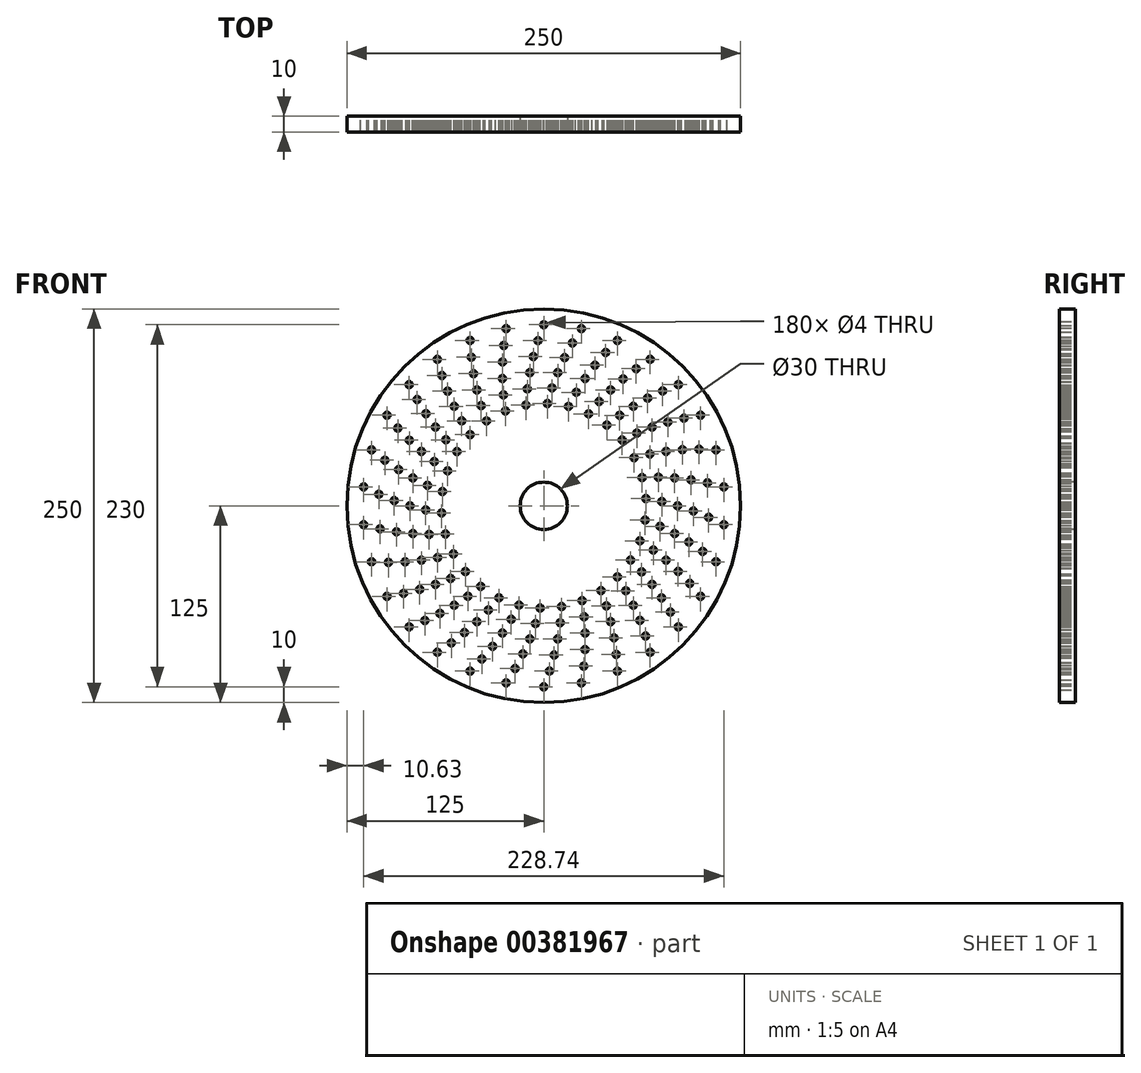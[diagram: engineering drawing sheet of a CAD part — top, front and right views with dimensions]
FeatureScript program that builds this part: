
annotation { "Feature Type Name" : "Feature", "Feature Type Description" : "" }
export const myFeature = defineFeature(function(context is Context, id is Id, definition is map)
    precondition{}
    {
        {
            var Q0;
            Q0=qCreatedBy(makeId("Front.planeOp"),FACE);
            var sketch = newSketch(context, id + "F0", { "sketchPlane" : qUnion([Q0])});
            skCircle(sketch, "E0", {"center": v(0, 0) * mm, "radius": 125 * mm});
            skCircle(sketch, "E1", {"center": v(0, 0) * mm, "radius": 115 * mm, "construction": true});
            skLineSegment(sketch, "E2", {"start": v(0, 125) * mm, "end": v(0, -125) * mm, "construction": true});
            skCircle(sketch, "E3", {"center": v(0, 115) * mm, "radius": 2 * mm});
            skCircle(sketch, "E4", {"center": v(0, 0) * mm, "radius": 105 * mm, "construction": true});
            skCircle(sketch, "E5", {"center": v(0, 0) * mm, "radius": 95 * mm, "construction": true});
            skCircle(sketch, "E6", {"center": v(0, 0) * mm, "radius": 85 * mm, "construction": true});
            skCircle(sketch, "E7", {"center": v(0, 0) * mm, "radius": 75 * mm, "construction": true});
            skCircle(sketch, "E8", {"center": v(0, 0) * mm, "radius": 65 * mm, "construction": true});
            skLineSegment(sketch, "E9", {"start": v(0, 0) * mm, "end": v(-3.66, 104.94) * mm, "construction": true});
            skLineSegment(sketch, "E10", {"start": v(0, 0) * mm, "end": v(-6.63, 94.77) * mm, "construction": true});
            skLineSegment(sketch, "E11", {"start": v(0, 0) * mm, "end": v(-8.88, 84.53) * mm, "construction": true});
            skLineSegment(sketch, "E12", {"start": v(0, 0) * mm, "end": v(-10.44, 74.27) * mm, "construction": true});
            skLineSegment(sketch, "E13", {"start": v(0, 0) * mm, "end": v(-11.29, 64.01) * mm, "construction": true});
            skCircle(sketch, "E14", {"center": v(-3.66, 104.94) * mm, "radius": 2 * mm});
            skCircle(sketch, "E15", {"center": v(-6.63, 94.77) * mm, "radius": 2 * mm});
            skCircle(sketch, "E16", {"center": v(-8.88, 84.53) * mm, "radius": 2 * mm});
            skCircle(sketch, "E17", {"center": v(-10.44, 74.27) * mm, "radius": 2 * mm});
            skCircle(sketch, "E18", {"center": v(-11.29, 64.01) * mm, "radius": 2 * mm});
            skCircle(sketch, "E19.1.0", {"center": v(-23.9, 112.49) * mm, "radius": 2 * mm});
            skCircle(sketch, "E19.1.1", {"center": v(-25.4, 101.88) * mm, "radius": 2 * mm});
            skCircle(sketch, "E19.1.2", {"center": v(-26.19, 91.32) * mm, "radius": 2 * mm});
            skCircle(sketch, "E19.1.3", {"center": v(-26.27, 80.84) * mm, "radius": 2 * mm});
            skCircle(sketch, "E19.1.4", {"center": v(-25.65, 70.48) * mm, "radius": 2 * mm});
            skCircle(sketch, "E19.1.5", {"center": v(-24.35, 60.27) * mm, "radius": 2 * mm});
            skCircle(sketch, "E19.2.0", {"center": v(-46.77, 105.06) * mm, "radius": 2 * mm});
            skCircle(sketch, "E19.2.1", {"center": v(-46.03, 94.37) * mm, "radius": 2 * mm});
            skCircle(sketch, "E19.2.2", {"center": v(-44.6, 83.88) * mm, "radius": 2 * mm});
            skCircle(sketch, "E19.2.3", {"center": v(-42.5, 73.61) * mm, "radius": 2 * mm});
            skCircle(sketch, "E19.2.4", {"center": v(-39.74, 63.6) * mm, "radius": 2 * mm});
            skCircle(sketch, "E19.2.5", {"center": v(-36.35, 53.89) * mm, "radius": 2 * mm});
            skCircle(sketch, "E19.3.0", {"center": v(-67.6, 93.04) * mm, "radius": 2 * mm});
            skCircle(sketch, "E19.3.1", {"center": v(-64.64, 82.74) * mm, "radius": 2 * mm});
            skCircle(sketch, "E19.3.2", {"center": v(-61.06, 72.77) * mm, "radius": 2 * mm});
            skCircle(sketch, "E19.3.3", {"center": v(-56.88, 63.17) * mm, "radius": 2 * mm});
            skCircle(sketch, "E19.3.4", {"center": v(-52.1, 53.95) * mm, "radius": 2 * mm});
            skCircle(sketch, "E19.3.5", {"center": v(-46.76, 45.15) * mm, "radius": 2 * mm});
            skCircle(sketch, "E19.4.0", {"center": v(-85.46, 76.95) * mm, "radius": 2 * mm});
            skCircle(sketch, "E19.4.1", {"center": v(-80.43, 67.5) * mm, "radius": 2 * mm});
            skCircle(sketch, "E19.4.2", {"center": v(-74.86, 58.49) * mm, "radius": 2 * mm});
            skCircle(sketch, "E19.4.3", {"center": v(-68.77, 49.96) * mm, "radius": 2 * mm});
            skCircle(sketch, "E19.4.4", {"center": v(-62.18, 41.94) * mm, "radius": 2 * mm});
            skCircle(sketch, "E19.4.5", {"center": v(-55.12, 34.44) * mm, "radius": 2 * mm});
            skCircle(sketch, "E19.5.0", {"center": v(-99.6, 57.5) * mm, "radius": 2 * mm});
            skCircle(sketch, "E19.5.1", {"center": v(-92.7, 49.3) * mm, "radius": 2 * mm});
            skCircle(sketch, "E19.5.2", {"center": v(-85.39, 41.65) * mm, "radius": 2 * mm});
            skCircle(sketch, "E19.5.3", {"center": v(-77.65, 34.57) * mm, "radius": 2 * mm});
            skCircle(sketch, "E19.5.4", {"center": v(-69.54, 28.1) * mm, "radius": 2 * mm});
            skCircle(sketch, "E19.5.5", {"center": v(-61.08, 22.23) * mm, "radius": 2 * mm});
            skCircle(sketch, "E19.6.0", {"center": v(-109.37, 35.54) * mm, "radius": 2 * mm});
            skCircle(sketch, "E19.6.1", {"center": v(-100.93, 28.94) * mm, "radius": 2 * mm});
            skCircle(sketch, "E19.6.2", {"center": v(-92.18, 22.98) * mm, "radius": 2 * mm});
            skCircle(sketch, "E19.6.3", {"center": v(-83.14, 17.67) * mm, "radius": 2 * mm});
            skCircle(sketch, "E19.6.4", {"center": v(-73.86, 13.02) * mm, "radius": 2 * mm});
            skCircle(sketch, "E19.6.5", {"center": v(-64.37, 9.05) * mm, "radius": 2 * mm});
            skCircle(sketch, "E19.7.0", {"center": v(-114.37, 12.02) * mm, "radius": 2 * mm});
            skCircle(sketch, "E19.7.1", {"center": v(-104.74, 7.32) * mm, "radius": 2 * mm});
            skCircle(sketch, "E19.7.2", {"center": v(-94.94, 3.32) * mm, "radius": 2 * mm});
            skCircle(sketch, "E19.7.3", {"center": v(-85, 0) * mm, "radius": 2 * mm});
            skCircle(sketch, "E19.7.4", {"center": v(-74.95, -2.62) * mm, "radius": 2 * mm});
            skCircle(sketch, "E19.7.5", {"center": v(-64.84, -4.53) * mm, "radius": 2 * mm});
            skCircle(sketch, "E19.8.0", {"center": v(-114.37, -12.02) * mm, "radius": 2 * mm});
            skCircle(sketch, "E19.8.1", {"center": v(-103.98, -14.61) * mm, "radius": 2 * mm});
            skCircle(sketch, "E19.8.2", {"center": v(-93.56, -16.5) * mm, "radius": 2 * mm});
            skCircle(sketch, "E19.8.3", {"center": v(-83.14, -17.67) * mm, "radius": 2 * mm});
            skCircle(sketch, "E19.8.4", {"center": v(-72.77, -18.14) * mm, "radius": 2 * mm});
            skCircle(sketch, "E19.8.5", {"center": v(-62.48, -17.92) * mm, "radius": 2 * mm});
            skCircle(sketch, "E19.9.0", {"center": v(-109.37, -35.54) * mm, "radius": 2 * mm});
            skCircle(sketch, "E19.9.1", {"center": v(-98.67, -35.91) * mm, "radius": 2 * mm});
            skCircle(sketch, "E19.9.2", {"center": v(-88.08, -35.59) * mm, "radius": 2 * mm});
            skCircle(sketch, "E19.9.3", {"center": v(-77.65, -34.57) * mm, "radius": 2 * mm});
            skCircle(sketch, "E19.9.4", {"center": v(-67.4, -32.88) * mm, "radius": 2 * mm});
            skCircle(sketch, "E19.9.5", {"center": v(-57.4, -30.52) * mm, "radius": 2 * mm});
            skCircle(sketch, "E19.10.0", {"center": v(-99.6, -57.5) * mm, "radius": 2 * mm});
            skCircle(sketch, "E19.10.1", {"center": v(-89.05, -55.64) * mm, "radius": 2 * mm});
            skCircle(sketch, "E19.10.2", {"center": v(-78.76, -53.12) * mm, "radius": 2 * mm});
            skCircle(sketch, "E19.10.3", {"center": v(-68.77, -49.96) * mm, "radius": 2 * mm});
            skCircle(sketch, "E19.10.4", {"center": v(-59.1, -46.17) * mm, "radius": 2 * mm});
            skCircle(sketch, "E19.10.5", {"center": v(-49.8, -41.78) * mm, "radius": 2 * mm});
            skCircle(sketch, "E19.11.0", {"center": v(-85.46, -76.95) * mm, "radius": 2 * mm});
            skCircle(sketch, "E19.11.1", {"center": v(-75.53, -72.94) * mm, "radius": 2 * mm});
            skCircle(sketch, "E19.11.2", {"center": v(-66, -68.34) * mm, "radius": 2 * mm});
            skCircle(sketch, "E19.11.3", {"center": v(-56.88, -63.17) * mm, "radius": 2 * mm});
            skCircle(sketch, "E19.11.4", {"center": v(-48.2, -57.45) * mm, "radius": 2 * mm});
            skCircle(sketch, "E19.11.5", {"center": v(-40.02, -51.22) * mm, "radius": 2 * mm});
            skCircle(sketch, "E19.12.0", {"center": v(-67.6, -93.04) * mm, "radius": 2 * mm});
            skCircle(sketch, "E19.12.1", {"center": v(-58.72, -87.05) * mm, "radius": 2 * mm});
            skCircle(sketch, "E19.12.2", {"center": v(-50.34, -80.56) * mm, "radius": 2 * mm});
            skCircle(sketch, "E19.12.3", {"center": v(-42.5, -73.61) * mm, "radius": 2 * mm});
            skCircle(sketch, "E19.12.4", {"center": v(-35.21, -66.22) * mm, "radius": 2 * mm});
            skCircle(sketch, "E19.12.5", {"center": v(-28.5, -58.42) * mm, "radius": 2 * mm});
            skCircle(sketch, "E19.13.0", {"center": v(-46.77, -105.06) * mm, "radius": 2 * mm});
            skCircle(sketch, "E19.13.1", {"center": v(-39.33, -97.35) * mm, "radius": 2 * mm});
            skCircle(sketch, "E19.13.2", {"center": v(-32.5, -89.27) * mm, "radius": 2 * mm});
            skCircle(sketch, "E19.13.3", {"center": v(-26.27, -80.84) * mm, "radius": 2 * mm});
            skCircle(sketch, "E19.13.4", {"center": v(-20.67, -72.1) * mm, "radius": 2 * mm});
            skCircle(sketch, "E19.13.5", {"center": v(-15.72, -63.07) * mm, "radius": 2 * mm});
            skCircle(sketch, "E19.14.0", {"center": v(-23.9, -112.49) * mm, "radius": 2 * mm});
            skCircle(sketch, "E19.14.1", {"center": v(-18.23, -103.4) * mm, "radius": 2 * mm});
            skCircle(sketch, "E19.14.2", {"center": v(-13.22, -94.08) * mm, "radius": 2 * mm});
            skCircle(sketch, "E19.14.3", {"center": v(-8.88, -84.53) * mm, "radius": 2 * mm});
            skCircle(sketch, "E19.14.4", {"center": v(-5.23, -74.82) * mm, "radius": 2 * mm});
            skCircle(sketch, "E19.14.5", {"center": v(-2.27, -64.96) * mm, "radius": 2 * mm});
            skCircle(sketch, "E19.15.0", {"center": v(0, -115) * mm, "radius": 2 * mm});
            skCircle(sketch, "E19.15.1", {"center": v(3.66, -104.94) * mm, "radius": 2 * mm});
            skCircle(sketch, "E19.15.2", {"center": v(6.63, -94.77) * mm, "radius": 2 * mm});
            skCircle(sketch, "E19.15.3", {"center": v(8.88, -84.53) * mm, "radius": 2 * mm});
            skCircle(sketch, "E19.15.4", {"center": v(10.44, -74.27) * mm, "radius": 2 * mm});
            skCircle(sketch, "E19.15.5", {"center": v(11.29, -64.01) * mm, "radius": 2 * mm});
            skCircle(sketch, "E19.16.0", {"center": v(23.9, -112.49) * mm, "radius": 2 * mm});
            skCircle(sketch, "E19.16.1", {"center": v(25.4, -101.88) * mm, "radius": 2 * mm});
            skCircle(sketch, "E19.16.2", {"center": v(26.19, -91.32) * mm, "radius": 2 * mm});
            skCircle(sketch, "E19.16.3", {"center": v(26.27, -80.84) * mm, "radius": 2 * mm});
            skCircle(sketch, "E19.16.4", {"center": v(25.65, -70.48) * mm, "radius": 2 * mm});
            skCircle(sketch, "E19.16.5", {"center": v(24.35, -60.27) * mm, "radius": 2 * mm});
            skCircle(sketch, "E19.17.0", {"center": v(46.77, -105.06) * mm, "radius": 2 * mm});
            skCircle(sketch, "E19.17.1", {"center": v(46.03, -94.37) * mm, "radius": 2 * mm});
            skCircle(sketch, "E19.17.2", {"center": v(44.6, -83.88) * mm, "radius": 2 * mm});
            skCircle(sketch, "E19.17.3", {"center": v(42.5, -73.61) * mm, "radius": 2 * mm});
            skCircle(sketch, "E19.17.4", {"center": v(39.74, -63.6) * mm, "radius": 2 * mm});
            skCircle(sketch, "E19.17.5", {"center": v(36.35, -53.89) * mm, "radius": 2 * mm});
            skCircle(sketch, "E19.18.0", {"center": v(67.6, -93.04) * mm, "radius": 2 * mm});
            skCircle(sketch, "E19.18.1", {"center": v(64.64, -82.74) * mm, "radius": 2 * mm});
            skCircle(sketch, "E19.18.2", {"center": v(61.06, -72.77) * mm, "radius": 2 * mm});
            skCircle(sketch, "E19.18.3", {"center": v(56.88, -63.17) * mm, "radius": 2 * mm});
            skCircle(sketch, "E19.18.4", {"center": v(52.1, -53.95) * mm, "radius": 2 * mm});
            skCircle(sketch, "E19.18.5", {"center": v(46.76, -45.15) * mm, "radius": 2 * mm});
            skCircle(sketch, "E19.19.0", {"center": v(85.46, -76.95) * mm, "radius": 2 * mm});
            skCircle(sketch, "E19.19.1", {"center": v(80.43, -67.5) * mm, "radius": 2 * mm});
            skCircle(sketch, "E19.19.2", {"center": v(74.86, -58.49) * mm, "radius": 2 * mm});
            skCircle(sketch, "E19.19.3", {"center": v(68.77, -49.96) * mm, "radius": 2 * mm});
            skCircle(sketch, "E19.19.4", {"center": v(62.18, -41.94) * mm, "radius": 2 * mm});
            skCircle(sketch, "E19.19.5", {"center": v(55.12, -34.44) * mm, "radius": 2 * mm});
            skCircle(sketch, "E19.20.0", {"center": v(99.6, -57.5) * mm, "radius": 2 * mm});
            skCircle(sketch, "E19.20.1", {"center": v(92.7, -49.3) * mm, "radius": 2 * mm});
            skCircle(sketch, "E19.20.2", {"center": v(85.39, -41.65) * mm, "radius": 2 * mm});
            skCircle(sketch, "E19.20.3", {"center": v(77.65, -34.57) * mm, "radius": 2 * mm});
            skCircle(sketch, "E19.20.4", {"center": v(69.54, -28.1) * mm, "radius": 2 * mm});
            skCircle(sketch, "E19.20.5", {"center": v(61.08, -22.23) * mm, "radius": 2 * mm});
            skCircle(sketch, "E19.21.0", {"center": v(109.37, -35.54) * mm, "radius": 2 * mm});
            skCircle(sketch, "E19.21.1", {"center": v(100.93, -28.94) * mm, "radius": 2 * mm});
            skCircle(sketch, "E19.21.2", {"center": v(92.18, -22.98) * mm, "radius": 2 * mm});
            skCircle(sketch, "E19.21.3", {"center": v(83.14, -17.67) * mm, "radius": 2 * mm});
            skCircle(sketch, "E19.21.4", {"center": v(73.86, -13.02) * mm, "radius": 2 * mm});
            skCircle(sketch, "E19.21.5", {"center": v(64.37, -9.05) * mm, "radius": 2 * mm});
            skCircle(sketch, "E19.22.0", {"center": v(114.37, -12.02) * mm, "radius": 2 * mm});
            skCircle(sketch, "E19.22.1", {"center": v(104.74, -7.32) * mm, "radius": 2 * mm});
            skCircle(sketch, "E19.22.2", {"center": v(94.94, -3.32) * mm, "radius": 2 * mm});
            skCircle(sketch, "E19.22.3", {"center": v(85, 0) * mm, "radius": 2 * mm});
            skCircle(sketch, "E19.22.4", {"center": v(74.95, 2.62) * mm, "radius": 2 * mm});
            skCircle(sketch, "E19.22.5", {"center": v(64.84, 4.53) * mm, "radius": 2 * mm});
            skCircle(sketch, "E19.23.0", {"center": v(114.37, 12.02) * mm, "radius": 2 * mm});
            skCircle(sketch, "E19.23.1", {"center": v(103.98, 14.61) * mm, "radius": 2 * mm});
            skCircle(sketch, "E19.23.2", {"center": v(93.56, 16.5) * mm, "radius": 2 * mm});
            skCircle(sketch, "E19.23.3", {"center": v(83.14, 17.67) * mm, "radius": 2 * mm});
            skCircle(sketch, "E19.23.4", {"center": v(72.77, 18.14) * mm, "radius": 2 * mm});
            skCircle(sketch, "E19.23.5", {"center": v(62.48, 17.92) * mm, "radius": 2 * mm});
            skCircle(sketch, "E19.24.0", {"center": v(109.37, 35.54) * mm, "radius": 2 * mm});
            skCircle(sketch, "E19.24.1", {"center": v(98.67, 35.91) * mm, "radius": 2 * mm});
            skCircle(sketch, "E19.24.2", {"center": v(88.08, 35.59) * mm, "radius": 2 * mm});
            skCircle(sketch, "E19.24.3", {"center": v(77.65, 34.57) * mm, "radius": 2 * mm});
            skCircle(sketch, "E19.24.4", {"center": v(67.4, 32.88) * mm, "radius": 2 * mm});
            skCircle(sketch, "E19.24.5", {"center": v(57.4, 30.52) * mm, "radius": 2 * mm});
            skCircle(sketch, "E19.25.0", {"center": v(99.6, 57.5) * mm, "radius": 2 * mm});
            skCircle(sketch, "E19.25.1", {"center": v(89.05, 55.64) * mm, "radius": 2 * mm});
            skCircle(sketch, "E19.25.2", {"center": v(78.76, 53.12) * mm, "radius": 2 * mm});
            skCircle(sketch, "E19.25.3", {"center": v(68.77, 49.96) * mm, "radius": 2 * mm});
            skCircle(sketch, "E19.25.4", {"center": v(59.1, 46.17) * mm, "radius": 2 * mm});
            skCircle(sketch, "E19.25.5", {"center": v(49.8, 41.78) * mm, "radius": 2 * mm});
            skCircle(sketch, "E19.26.0", {"center": v(85.46, 76.95) * mm, "radius": 2 * mm});
            skCircle(sketch, "E19.26.1", {"center": v(75.53, 72.94) * mm, "radius": 2 * mm});
            skCircle(sketch, "E19.26.2", {"center": v(66, 68.34) * mm, "radius": 2 * mm});
            skCircle(sketch, "E19.26.3", {"center": v(56.88, 63.17) * mm, "radius": 2 * mm});
            skCircle(sketch, "E19.26.4", {"center": v(48.2, 57.45) * mm, "radius": 2 * mm});
            skCircle(sketch, "E19.26.5", {"center": v(40.02, 51.22) * mm, "radius": 2 * mm});
            skCircle(sketch, "E19.27.0", {"center": v(67.6, 93.04) * mm, "radius": 2 * mm});
            skCircle(sketch, "E19.27.1", {"center": v(58.72, 87.05) * mm, "radius": 2 * mm});
            skCircle(sketch, "E19.27.2", {"center": v(50.34, 80.56) * mm, "radius": 2 * mm});
            skCircle(sketch, "E19.27.3", {"center": v(42.5, 73.61) * mm, "radius": 2 * mm});
            skCircle(sketch, "E19.27.4", {"center": v(35.21, 66.22) * mm, "radius": 2 * mm});
            skCircle(sketch, "E19.27.5", {"center": v(28.5, 58.42) * mm, "radius": 2 * mm});
            skCircle(sketch, "E19.28.0", {"center": v(46.77, 105.06) * mm, "radius": 2 * mm});
            skCircle(sketch, "E19.28.1", {"center": v(39.33, 97.35) * mm, "radius": 2 * mm});
            skCircle(sketch, "E19.28.2", {"center": v(32.5, 89.27) * mm, "radius": 2 * mm});
            skCircle(sketch, "E19.28.3", {"center": v(26.27, 80.84) * mm, "radius": 2 * mm});
            skCircle(sketch, "E19.28.4", {"center": v(20.67, 72.1) * mm, "radius": 2 * mm});
            skCircle(sketch, "E19.28.5", {"center": v(15.72, 63.07) * mm, "radius": 2 * mm});
            skCircle(sketch, "E19.29.0", {"center": v(23.9, 112.49) * mm, "radius": 2 * mm});
            skCircle(sketch, "E19.29.1", {"center": v(18.23, 103.4) * mm, "radius": 2 * mm});
            skCircle(sketch, "E19.29.2", {"center": v(13.22, 94.08) * mm, "radius": 2 * mm});
            skCircle(sketch, "E19.29.3", {"center": v(8.88, 84.53) * mm, "radius": 2 * mm});
            skCircle(sketch, "E19.29.4", {"center": v(5.23, 74.82) * mm, "radius": 2 * mm});
            skCircle(sketch, "E19.29.5", {"center": v(2.27, 64.96) * mm, "radius": 2 * mm});
            skSolve(sketch);
        }
        {
            var Q0;
            Q0=makeQuery(id+"F0.imprint","IMPRINT",FACE,{"disambiguationData":[TD([[makeQuery(id+"F0.imprint","IMPRINT",EDGE,{"derivedFrom":sQuery(id+"F0.wireOp",EDGE,"E0")}),1.0]])]});
            extrude(context, id + "F1", {"entities" : qUnion([Q0]), "depth" : 10 * mm});
        }
        {
            var Q0;
            Q0=makeQuery(id+"F1.opExtrude","CAP_FACE",FACE,{"disambiguationData":[OSD([sQuery(id+"F0.wireOp",EDGE,"E0"),sQuery(id+"F0.wireOp",EDGE,"E3"),sQuery(id+"F0.wireOp",EDGE,"E14"),sQuery(id+"F0.wireOp",EDGE,"E15"),sQuery(id+"F0.wireOp",EDGE,"E16"),sQuery(id+"F0.wireOp",EDGE,"E17"),sQuery(id+"F0.wireOp",EDGE,"E18"),sQuery(id+"F0.wireOp",EDGE,"E19.1.0"),sQuery(id+"F0.wireOp",EDGE,"E19.1.1"),sQuery(id+"F0.wireOp",EDGE,"E19.1.2"),sQuery(id+"F0.wireOp",EDGE,"E19.1.3"),sQuery(id+"F0.wireOp",EDGE,"E19.1.4"),sQuery(id+"F0.wireOp",EDGE,"E19.1.5"),sQuery(id+"F0.wireOp",EDGE,"E19.2.0"),sQuery(id+"F0.wireOp",EDGE,"E19.2.1"),sQuery(id+"F0.wireOp",EDGE,"E19.2.2"),sQuery(id+"F0.wireOp",EDGE,"E19.2.3"),sQuery(id+"F0.wireOp",EDGE,"E19.2.4"),sQuery(id+"F0.wireOp",EDGE,"E19.2.5"),sQuery(id+"F0.wireOp",EDGE,"E19.3.0"),sQuery(id+"F0.wireOp",EDGE,"E19.3.1"),sQuery(id+"F0.wireOp",EDGE,"E19.3.2"),sQuery(id+"F0.wireOp",EDGE,"E19.3.3"),sQuery(id+"F0.wireOp",EDGE,"E19.3.4"),sQuery(id+"F0.wireOp",EDGE,"E19.3.5"),sQuery(id+"F0.wireOp",EDGE,"E19.4.0"),sQuery(id+"F0.wireOp",EDGE,"E19.4.1"),sQuery(id+"F0.wireOp",EDGE,"E19.4.2"),sQuery(id+"F0.wireOp",EDGE,"E19.4.3"),sQuery(id+"F0.wireOp",EDGE,"E19.4.4"),sQuery(id+"F0.wireOp",EDGE,"E19.4.5"),sQuery(id+"F0.wireOp",EDGE,"E19.5.0"),sQuery(id+"F0.wireOp",EDGE,"E19.5.1"),sQuery(id+"F0.wireOp",EDGE,"E19.5.2"),sQuery(id+"F0.wireOp",EDGE,"E19.5.3"),sQuery(id+"F0.wireOp",EDGE,"E19.5.4"),sQuery(id+"F0.wireOp",EDGE,"E19.5.5"),sQuery(id+"F0.wireOp",EDGE,"E19.6.0"),sQuery(id+"F0.wireOp",EDGE,"E19.6.1"),sQuery(id+"F0.wireOp",EDGE,"E19.6.2"),sQuery(id+"F0.wireOp",EDGE,"E19.6.3"),sQuery(id+"F0.wireOp",EDGE,"E19.6.4"),sQuery(id+"F0.wireOp",EDGE,"E19.6.5"),sQuery(id+"F0.wireOp",EDGE,"E19.7.0"),sQuery(id+"F0.wireOp",EDGE,"E19.7.1"),sQuery(id+"F0.wireOp",EDGE,"E19.7.2"),sQuery(id+"F0.wireOp",EDGE,"E19.7.3"),sQuery(id+"F0.wireOp",EDGE,"E19.7.4"),sQuery(id+"F0.wireOp",EDGE,"E19.7.5"),sQuery(id+"F0.wireOp",EDGE,"E19.8.0"),sQuery(id+"F0.wireOp",EDGE,"E19.8.1"),sQuery(id+"F0.wireOp",EDGE,"E19.8.2"),sQuery(id+"F0.wireOp",EDGE,"E19.8.3"),sQuery(id+"F0.wireOp",EDGE,"E19.8.4"),sQuery(id+"F0.wireOp",EDGE,"E19.8.5"),sQuery(id+"F0.wireOp",EDGE,"E19.9.0"),sQuery(id+"F0.wireOp",EDGE,"E19.9.1"),sQuery(id+"F0.wireOp",EDGE,"E19.9.2"),sQuery(id+"F0.wireOp",EDGE,"E19.9.3"),sQuery(id+"F0.wireOp",EDGE,"E19.9.4"),sQuery(id+"F0.wireOp",EDGE,"E19.9.5"),sQuery(id+"F0.wireOp",EDGE,"E19.10.0"),sQuery(id+"F0.wireOp",EDGE,"E19.10.1"),sQuery(id+"F0.wireOp",EDGE,"E19.10.2"),sQuery(id+"F0.wireOp",EDGE,"E19.10.3"),sQuery(id+"F0.wireOp",EDGE,"E19.10.4"),sQuery(id+"F0.wireOp",EDGE,"E19.10.5"),sQuery(id+"F0.wireOp",EDGE,"E19.11.0"),sQuery(id+"F0.wireOp",EDGE,"E19.11.1"),sQuery(id+"F0.wireOp",EDGE,"E19.11.2"),sQuery(id+"F0.wireOp",EDGE,"E19.11.3"),sQuery(id+"F0.wireOp",EDGE,"E19.11.4"),sQuery(id+"F0.wireOp",EDGE,"E19.11.5"),sQuery(id+"F0.wireOp",EDGE,"E19.12.0"),sQuery(id+"F0.wireOp",EDGE,"E19.12.1"),sQuery(id+"F0.wireOp",EDGE,"E19.12.2"),sQuery(id+"F0.wireOp",EDGE,"E19.12.3"),sQuery(id+"F0.wireOp",EDGE,"E19.12.4"),sQuery(id+"F0.wireOp",EDGE,"E19.12.5"),sQuery(id+"F0.wireOp",EDGE,"E19.13.0"),sQuery(id+"F0.wireOp",EDGE,"E19.13.1"),sQuery(id+"F0.wireOp",EDGE,"E19.13.2"),sQuery(id+"F0.wireOp",EDGE,"E19.13.3"),sQuery(id+"F0.wireOp",EDGE,"E19.13.4"),sQuery(id+"F0.wireOp",EDGE,"E19.13.5"),sQuery(id+"F0.wireOp",EDGE,"E19.14.0"),sQuery(id+"F0.wireOp",EDGE,"E19.14.1"),sQuery(id+"F0.wireOp",EDGE,"E19.14.2"),sQuery(id+"F0.wireOp",EDGE,"E19.14.3"),sQuery(id+"F0.wireOp",EDGE,"E19.14.4"),sQuery(id+"F0.wireOp",EDGE,"E19.14.5"),sQuery(id+"F0.wireOp",EDGE,"E19.15.0"),sQuery(id+"F0.wireOp",EDGE,"E19.15.1"),sQuery(id+"F0.wireOp",EDGE,"E19.15.2"),sQuery(id+"F0.wireOp",EDGE,"E19.15.3"),sQuery(id+"F0.wireOp",EDGE,"E19.15.4"),sQuery(id+"F0.wireOp",EDGE,"E19.15.5"),sQuery(id+"F0.wireOp",EDGE,"E19.16.0"),sQuery(id+"F0.wireOp",EDGE,"E19.16.1"),sQuery(id+"F0.wireOp",EDGE,"E19.16.2"),sQuery(id+"F0.wireOp",EDGE,"E19.16.3"),sQuery(id+"F0.wireOp",EDGE,"E19.16.4"),sQuery(id+"F0.wireOp",EDGE,"E19.16.5"),sQuery(id+"F0.wireOp",EDGE,"E19.17.0"),sQuery(id+"F0.wireOp",EDGE,"E19.17.1"),sQuery(id+"F0.wireOp",EDGE,"E19.17.2"),sQuery(id+"F0.wireOp",EDGE,"E19.17.3"),sQuery(id+"F0.wireOp",EDGE,"E19.17.4"),sQuery(id+"F0.wireOp",EDGE,"E19.17.5"),sQuery(id+"F0.wireOp",EDGE,"E19.18.0"),sQuery(id+"F0.wireOp",EDGE,"E19.18.1"),sQuery(id+"F0.wireOp",EDGE,"E19.18.2"),sQuery(id+"F0.wireOp",EDGE,"E19.18.3"),sQuery(id+"F0.wireOp",EDGE,"E19.18.4"),sQuery(id+"F0.wireOp",EDGE,"E19.18.5"),sQuery(id+"F0.wireOp",EDGE,"E19.19.0"),sQuery(id+"F0.wireOp",EDGE,"E19.19.1"),sQuery(id+"F0.wireOp",EDGE,"E19.19.2"),sQuery(id+"F0.wireOp",EDGE,"E19.19.3"),sQuery(id+"F0.wireOp",EDGE,"E19.19.4"),sQuery(id+"F0.wireOp",EDGE,"E19.19.5"),sQuery(id+"F0.wireOp",EDGE,"E19.20.0"),sQuery(id+"F0.wireOp",EDGE,"E19.20.1"),sQuery(id+"F0.wireOp",EDGE,"E19.20.2"),sQuery(id+"F0.wireOp",EDGE,"E19.20.3"),sQuery(id+"F0.wireOp",EDGE,"E19.20.4"),sQuery(id+"F0.wireOp",EDGE,"E19.20.5"),sQuery(id+"F0.wireOp",EDGE,"E19.21.0"),sQuery(id+"F0.wireOp",EDGE,"E19.21.1"),sQuery(id+"F0.wireOp",EDGE,"E19.21.2"),sQuery(id+"F0.wireOp",EDGE,"E19.21.3"),sQuery(id+"F0.wireOp",EDGE,"E19.21.4"),sQuery(id+"F0.wireOp",EDGE,"E19.21.5"),sQuery(id+"F0.wireOp",EDGE,"E19.22.0"),sQuery(id+"F0.wireOp",EDGE,"E19.22.1"),sQuery(id+"F0.wireOp",EDGE,"E19.22.2"),sQuery(id+"F0.wireOp",EDGE,"E19.22.3"),sQuery(id+"F0.wireOp",EDGE,"E19.22.4"),sQuery(id+"F0.wireOp",EDGE,"E19.22.5"),sQuery(id+"F0.wireOp",EDGE,"E19.23.0"),sQuery(id+"F0.wireOp",EDGE,"E19.23.1"),sQuery(id+"F0.wireOp",EDGE,"E19.23.2"),sQuery(id+"F0.wireOp",EDGE,"E19.23.3"),sQuery(id+"F0.wireOp",EDGE,"E19.23.4"),sQuery(id+"F0.wireOp",EDGE,"E19.23.5"),sQuery(id+"F0.wireOp",EDGE,"E19.24.0"),sQuery(id+"F0.wireOp",EDGE,"E19.24.1"),sQuery(id+"F0.wireOp",EDGE,"E19.24.2"),sQuery(id+"F0.wireOp",EDGE,"E19.24.3"),sQuery(id+"F0.wireOp",EDGE,"E19.24.4"),sQuery(id+"F0.wireOp",EDGE,"E19.24.5"),sQuery(id+"F0.wireOp",EDGE,"E19.25.0"),sQuery(id+"F0.wireOp",EDGE,"E19.25.1"),sQuery(id+"F0.wireOp",EDGE,"E19.25.2"),sQuery(id+"F0.wireOp",EDGE,"E19.25.3"),sQuery(id+"F0.wireOp",EDGE,"E19.25.4"),sQuery(id+"F0.wireOp",EDGE,"E19.25.5"),sQuery(id+"F0.wireOp",EDGE,"E19.26.0"),sQuery(id+"F0.wireOp",EDGE,"E19.26.1"),sQuery(id+"F0.wireOp",EDGE,"E19.26.2"),sQuery(id+"F0.wireOp",EDGE,"E19.26.3"),sQuery(id+"F0.wireOp",EDGE,"E19.26.4"),sQuery(id+"F0.wireOp",EDGE,"E19.26.5"),sQuery(id+"F0.wireOp",EDGE,"E19.27.0"),sQuery(id+"F0.wireOp",EDGE,"E19.27.1"),sQuery(id+"F0.wireOp",EDGE,"E19.27.2"),sQuery(id+"F0.wireOp",EDGE,"E19.27.3"),sQuery(id+"F0.wireOp",EDGE,"E19.27.4"),sQuery(id+"F0.wireOp",EDGE,"E19.27.5"),sQuery(id+"F0.wireOp",EDGE,"E19.28.0"),sQuery(id+"F0.wireOp",EDGE,"E19.28.1"),sQuery(id+"F0.wireOp",EDGE,"E19.28.2"),sQuery(id+"F0.wireOp",EDGE,"E19.28.3"),sQuery(id+"F0.wireOp",EDGE,"E19.28.4"),sQuery(id+"F0.wireOp",EDGE,"E19.28.5"),sQuery(id+"F0.wireOp",EDGE,"E19.29.0"),sQuery(id+"F0.wireOp",EDGE,"E19.29.1"),sQuery(id+"F0.wireOp",EDGE,"E19.29.2"),sQuery(id+"F0.wireOp",EDGE,"E19.29.3"),sQuery(id+"F0.wireOp",EDGE,"E19.29.4"),sQuery(id+"F0.wireOp",EDGE,"E19.29.5")])],"isStart":false});
            var sketch = newSketch(context, id + "F2", { "sketchPlane" : qUnion([Q0])});
            skCircle(sketch, "E20", {"center": v(0, 0) * mm, "radius": 15 * mm});
            skSolve(sketch);
        }
        {
            var Q0;
            Q0=makeQuery(id+"F2.imprint","IMPRINT",FACE,{"disambiguationData":[TD([[makeQuery(id+"F2.imprint","IMPRINT",EDGE,{"derivedFrom":sQuery(id+"F2.wireOp",EDGE,"E20")}),1.0]])]});
            extrude(context, id + "F3", {"entities" : qUnion([Q0]), "operationType" : NewBodyOperationType.REMOVE, "oppositeDirection" : true, "depth" : 25 * mm});
        }
    });
